FCSTD DOCUMENT  (FreeCAD 0.16R6710 (Git))
Label: cross_sect_blocks
License: All rights reserved
LicenseURL: http://en.wikipedia.org/wiki/All_rights_reserved
objects: Part::FeaturePython×7, Part::Part2DObjectPython×6
note: 13 computed .brp shape members not serialized (recipe doc carries the construction recipe); baked Part::Feature solids carry a one-line shape summary decoded from their .brp

FEATURE [Part::Part2DObjectPython] DWire  # Draft 2D object (typed FeaturePython)
  ChamferSize = 0
  Closed = true
  End = (39673.9,13491.1,0)
  FilletRadius = 0
  Length = 33.9027
  MakeFace = true
  Points = (12) [(39673.4,13491.6,0),(39673.4,13496.4,0),(39673.6,13496.6,0),(39678.2,13496.5,0),(39678.4,13496.3,0),(39678.4,13494.5,0),(39685.4,13493.5,0),+5 more]
  Start = (39673.4,13491.6,0)
  Subdivisions = 0
FEATURE [Part::Part2DObjectPython] DWire001  # Draft 2D object (typed FeaturePython)
  ChamferSize = 0
  Closed = true
  End = (39685,13491,0)
  FilletRadius = 0
  Length = 37.5101
  MakeFace = true
  Points = (6) [(39685.4,13493.5,0),(39691.2,13492.6,0),(39701.4,13492.3,0),(39701.4,13489.8,0),(39691,13490.1,0),(39685,13491,0)]
  Start = (39685.4,13493.5,0)
  Subdivisions = 0
FEATURE [Part::Part2DObjectPython] DWire002  # Draft 2D object (typed FeaturePython)
  ChamferSize = 0
  Closed = true
  End = (39701.4,13489.8,0)
  FilletRadius = 0
  Length = 37.4353
  MakeFace = true
  Points = (4) [(39701.4,13492.3,0),(39717.7,13491.8,0),(39717.6,13489.3,0),(39701.4,13489.8,0)]
  Start = (39701.4,13492.3,0)
  Subdivisions = 0
FEATURE [Part::Part2DObjectPython] DWire003  # Draft 2D object (typed FeaturePython)
  ChamferSize = 0
  Closed = true
  End = (39717.6,13489.3,0)
  FilletRadius = 0
  Length = 37.4353
  MakeFace = true
  Points = (4) [(39717.7,13491.8,0),(39733.9,13491.3,0),(39733.8,13488.8,0),(39717.6,13489.3,0)]
  Start = (39717.7,13491.8,0)
  Subdivisions = 0
FEATURE [Part::Part2DObjectPython] DWire004  # Draft 2D object (typed FeaturePython)
  ChamferSize = 0
  Closed = true
  End = (39733.8,13488.8,0)
  FilletRadius = 0
  Length = 37.4353
  MakeFace = true
  Points = (4) [(39733.9,13491.3,0),(39750.1,13490.8,0),(39750,13488.3,0),(39733.8,13488.8,0)]
  Start = (39733.9,13491.3,0)
  Subdivisions = 0
FEATURE [Part::Part2DObjectPython] DWire005  # Draft 2D object (typed FeaturePython)
  ChamferSize = 0
  Closed = true
  End = (39750,13488.3,0)
  FilletRadius = 0
  Length = 30.9551
  MakeFace = true
  Points = (13) [(39750.1,13490.8,0),(39754.7,13490.7,0),(39754.9,13490.9,0),(39755,13493.2,0),(39754.9,13493.6,0),(39755.1,13493.8,0),(39759.7,13493.9,0),+6 more]
  Start = (39750.1,13490.8,0)
  Subdivisions = 0
FEATURE [Part::FeaturePython] Point001  # WARN: FeaturePython — macro-defined, semantics opaque (R4)
  X = 39678.4
  Y = 13493.6
  Z = 0
FEATURE [Part::FeaturePython] Point002  # WARN: FeaturePython — macro-defined, semantics opaque (R4)
  X = 39693.3
  Y = 13491.4
  Z = 0
FEATURE [Part::FeaturePython] Point003  # WARN: FeaturePython — macro-defined, semantics opaque (R4)
  X = 39709.5
  Y = 13490.8
  Z = 0
FEATURE [Part::FeaturePython] Point004  # WARN: FeaturePython — macro-defined, semantics opaque (R4)
  X = 39725.7
  Y = 13490.3
  Z = 0
FEATURE [Part::FeaturePython] Point005  # WARN: FeaturePython — macro-defined, semantics opaque (R4)
  X = 39741.9
  Y = 13489.8
  Z = 0
FEATURE [Part::FeaturePython] Point006  # WARN: FeaturePython — macro-defined, semantics opaque (R4)
  X = 39755.9
  Y = 13490.6
  Z = 0
FEATURE [Part::FeaturePython] Point  # WARN: FeaturePython — macro-defined, semantics opaque (R4)
  X = 39673.9
  Y = 13491.1
  Z = 0
